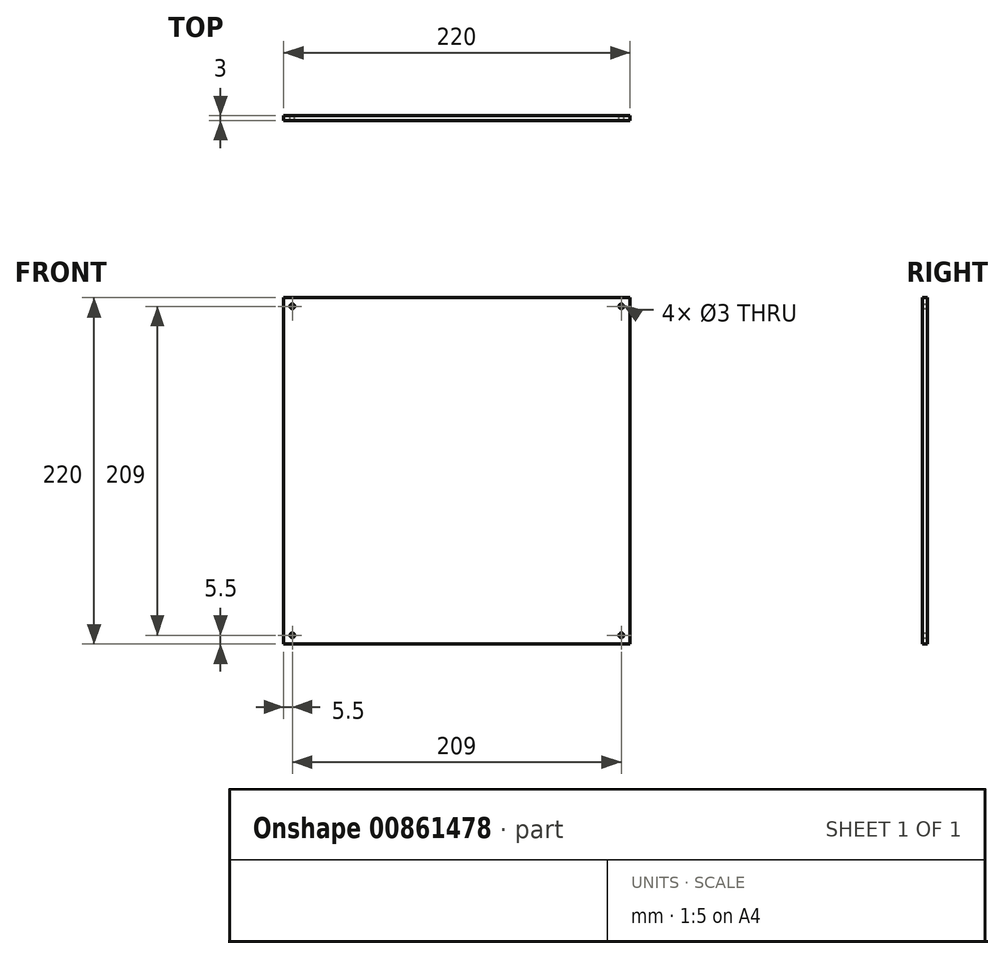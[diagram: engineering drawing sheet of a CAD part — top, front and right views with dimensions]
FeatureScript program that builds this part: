
annotation { "Feature Type Name" : "Feature", "Feature Type Description" : "" }
export const myFeature = defineFeature(function(context is Context, id is Id, definition is map)
    precondition{}
    {
        {
            var Q0;
            Q0=qCreatedBy(makeId("Front.planeOp"),FACE);
            var sketch = newSketch(context, id + "F0", { "sketchPlane" : qUnion([Q0])});
            skLineSegment(sketch, "E0.bottom", {"start": v(110, 110) * mm, "end": v(-110, 110) * mm});
            skLineSegment(sketch, "E0.top", {"start": v(110, -110) * mm, "end": v(-110, -110) * mm});
            skLineSegment(sketch, "E0.left", {"start": v(110, 110) * mm, "end": v(110, -110) * mm});
            skLineSegment(sketch, "E0.right", {"start": v(-110, 110) * mm, "end": v(-110, -110) * mm});
            skPoint(sketch, "E0.middle", {"position": v(0, 0) * mm});
            skLineSegment(sketch, "E1.1", {"start": v(104.5, 104.5) * mm, "end": v(104.5, -104.5) * mm, "construction": true});
            skLineSegment(sketch, "E1.2", {"start": v(104.5, -104.5) * mm, "end": v(-104.5, -104.5) * mm, "construction": true});
            skLineSegment(sketch, "E1.3", {"start": v(-104.5, 104.5) * mm, "end": v(-104.5, -104.5) * mm, "construction": true});
            skLineSegment(sketch, "E2", {"start": v(-104.5, 104.5) * mm, "end": v(104.5, 104.5) * mm, "construction": true});
            skPoint(sketch, "E3", {"position": v(-104.5, 104.5) * mm});
            skPoint(sketch, "E4", {"position": v(104.5, 104.5) * mm});
            skPoint(sketch, "E5", {"position": v(104.5, -104.5) * mm});
            skPoint(sketch, "E6", {"position": v(-104.5, -104.5) * mm});
            skSolve(sketch);
        }
        {
            var Q0;
            Q0=qSketchRegion(id+"F0",true);
            extrude(context, id + "F1", {"entities" : qUnion([Q0]), "depth" : 3 * mm, "offsetDistance" : 25 * mm});
        }
        {
            var Q0;
            Q0=sQuery(id+"F0.wireOp",VERTEX,"E3");
            var Q1;
            Q1=sQuery(id+"F0.wireOp",VERTEX,"E4");
            var Q2;
            Q2=sQuery(id+"F0.wireOp",VERTEX,"E5");
            var Q3;
            Q3=sQuery(id+"F0.wireOp",VERTEX,"E6");
            var Q4;
            Q4=makeQuery(id+"F1.opExtrude","SWEPT_BODY",BODY,{"disambiguationData":[OSD([sQuery(id+"F0.wireOp",EDGE,"E0.bottom"),sQuery(id+"F0.wireOp",EDGE,"E0.top"),sQuery(id+"F0.wireOp",EDGE,"E0.left"),sQuery(id+"F0.wireOp",EDGE,"E0.right")])]});
            hole(context, id + "F2", {"style" : HoleStyle.SIMPLE, "endStyle" : HoleEndStyle.BLIND, "oppositeDirection" : true, "holeDiameter" : 3 * mm, "majorDiameter" : 5 * mm, "holeDepth" : 10 * mm, "isTappedThrough" : true, "tappedDepth" : 12 * mm, "tapClearance" : 3, "locations" : qUnion([Q0, Q1, Q2, Q3]), "scope" : qUnion([Q4])});
        }
    });
